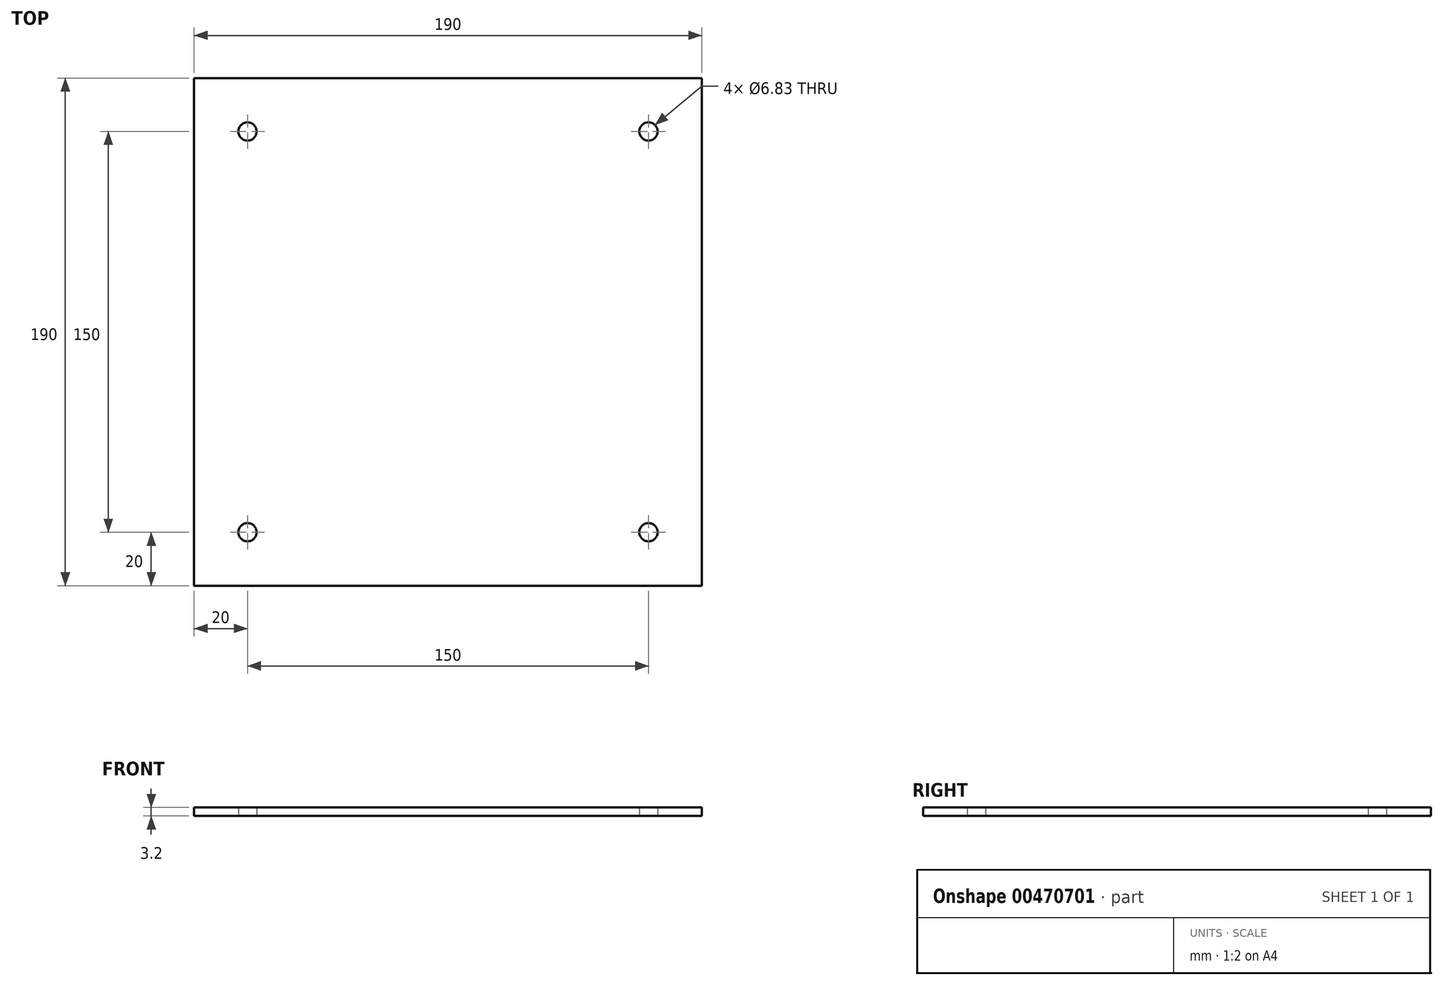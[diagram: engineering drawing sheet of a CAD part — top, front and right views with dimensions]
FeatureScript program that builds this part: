
annotation { "Feature Type Name" : "Feature", "Feature Type Description" : "" }
export const myFeature = defineFeature(function(context is Context, id is Id, definition is map)
    precondition{}
    {
        {
            var Q0;
            Q0=qCreatedBy(makeId("Top.planeOp"),FACE);
            var sketch = newSketch(context, id + "F0", { "sketchPlane" : qUnion([Q0])});
            skLineSegment(sketch, "E0.bottom", {"start": v(-95, 95) * mm, "end": v(95, 95) * mm});
            skLineSegment(sketch, "E0.top", {"start": v(-95, -95) * mm, "end": v(95, -95) * mm});
            skLineSegment(sketch, "E0.left", {"start": v(-95, 95) * mm, "end": v(-95, -95) * mm});
            skLineSegment(sketch, "E0.right", {"start": v(95, 95) * mm, "end": v(95, -95) * mm});
            skPoint(sketch, "E0.middle", {"position": v(0, 0) * mm});
            skCircle(sketch, "E1", {"center": v(-75, -75) * mm, "radius": 3.41 * mm});
            skCircle(sketch, "E2", {"center": v(-75, 75) * mm, "radius": 3.41 * mm});
            skCircle(sketch, "E3", {"center": v(75, 75) * mm, "radius": 3.41 * mm});
            skCircle(sketch, "E4", {"center": v(75, -75) * mm, "radius": 3.41 * mm});
            skCircle(sketch, "E5", {"center": v(0, 0) * mm, "radius": 49.75 * mm});
            skSolve(sketch);
        }
        {
            var Q0;
            Q0=makeQuery(id+"F0.imprint","IMPRINT",FACE,{"disambiguationData":[TD([[makeQuery(id+"F0.imprint","IMPRINT",EDGE,{"derivedFrom":sQuery(id+"F0.wireOp",EDGE,"E0.bottom")}),-1.0]])]});
            var Q1;
            Q1=makeQuery(id+"F0.imprint","IMPRINT",FACE,{"disambiguationData":[TD([[makeQuery(id+"F0.imprint","IMPRINT",EDGE,{"derivedFrom":sQuery(id+"F0.wireOp",EDGE,"E5")}),1.0]])]});
            extrude(context, id + "F1", {"entities" : qUnion([Q0, Q1]), "depth" : 3.2 * mm});
        }
    });
